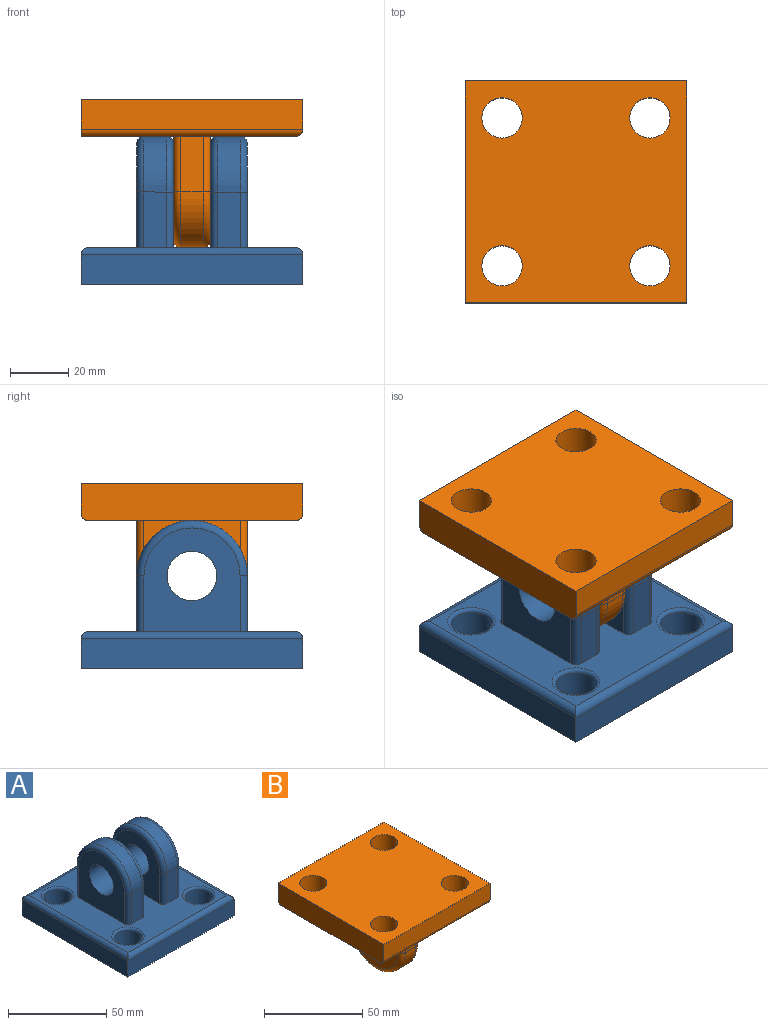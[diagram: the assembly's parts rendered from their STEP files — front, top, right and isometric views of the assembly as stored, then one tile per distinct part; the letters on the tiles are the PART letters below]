
ASSEMBLY  parts=2 mates=1
PART A: 42 faces, bbox 76.2x76.2x52.4 mm
  f0: plane 19.05x7.62mm, normal (0,-1,0), area 145.2mm2, adj f3,f5,f27,f28
  f1: plane 19.05x7.62mm, normal (0,1,0), area 145.2mm2, adj f3,f5,f25,f30
  f2: cylinder r=19.05mm len=38.1mm, axis (1,0,0), area 456mm2, adj f16,f18,f23,f32
  f3: cylinder r=19.05mm len=38.1mm, axis (1,0,0), area 456mm2, adj f0,f1,f26,f29
  f4: cylinder r=8.54mm len=17.08mm, axis (1,0,0), area 681.5mm2, adj f15,f20
  f5: plane 71.12x71.12mm, normal (0,0,1), area 3258.5mm2, adj f0,f1,f15,f16,f17,f18,f20,f21
  f6: plane 76.2x10.16mm, normal (0,-1,0), area 774.2mm2, adj f7,f13,f14,f34
  f7: plane 76.2x10.16mm, normal (1,0,0), area 774.2mm2, adj f6,f8,f14,f35
  f8: plane 76.2x10.16mm, normal (0,1,0), area 774.2mm2, adj f7,f13,f14,f37
  f9: cylinder r=6.92mm len=13.84mm, axis (0,0,-1), area 497mm2, adj f14,f41
  f10: cylinder r=6.92mm len=13.84mm, axis (0,0,-1), area 497mm2, adj f14,f40
  f11: cylinder r=6.92mm len=13.84mm, axis (0,0,-1), area 497mm2, adj f14,f39
  f12: cylinder r=6.92mm len=13.84mm, axis (0,0,-1), area 497mm2, adj f14,f38
  f13: plane 76.2x10.16mm, normal (-1,0,0), area 774.2mm2, adj f6,f8,f14,f36
  f14: plane 76.2x76.2mm, normal (0,0,-1), area 5204.7mm2, adj f6,f7,f8,f9,f10,f11,f12,f13
  f15: plane 35.56x33.02mm, normal (-1,0,0), area 828.1mm2, adj f4,f5,f31,f32,f33
  f16: plane 19.05x7.62mm, normal (0,-1,0), area 145.2mm2, adj f2,f5,f24,f31
  f17: plane 35.56x33.02mm, normal (1,0,0), area 828.1mm2, adj f5,f19,f28,f29,f30
  f18: plane 19.05x7.62mm, normal (0,1,0), area 145.2mm2, adj f2,f5,f22,f33
  f19: cylinder r=8.54mm len=17.08mm, axis (1,0,0), area 681.5mm2, adj f17,f21
  f20: plane 35.56x33.02mm, normal (1,0,0), area 828.1mm2, adj f4,f5,f22,f23,f24
  f21: plane 35.56x33.02mm, normal (-1,0,0), area 828.1mm2, adj f5,f19,f25,f26,f27
  f22: cylinder r=2.54mm len=19.05mm, axis (0,0,1), area 76mm2, adj f5,f18,f20,f23
  f23: torus R=16.51mm, axis (1,0,0), area 227.2mm2, adj f2,f20,f22,f24
  f24: cylinder r=2.54mm len=19.05mm, axis (0,0,-1), area 76mm2, adj f5,f16,f20,f23
  f25: cylinder r=2.54mm len=19.05mm, axis (0,0,-1), area 76mm2, adj f1,f5,f21,f26
  f26: torus R=16.51mm, axis (1,0,0), area 227.2mm2, adj f3,f21,f25,f27
  f27: cylinder r=2.54mm len=19.05mm, axis (0,0,1), area 76mm2, adj f0,f5,f21,f26
  f28: cylinder r=2.54mm len=19.05mm, axis (0,0,-1), area 76mm2, adj f0,f5,f17,f29
  f29: torus R=16.51mm, axis (-1,0,0), area 227.2mm2, adj f3,f17,f28,f30
  f30: cylinder r=2.54mm len=19.05mm, axis (0,0,1), area 76mm2, adj f1,f5,f17,f29
  f31: cylinder r=2.54mm len=19.05mm, axis (0,0,1), area 76mm2, adj f5,f15,f16,f32
  f32: torus R=16.51mm, axis (-1,0,0), area 227.2mm2, adj f2,f15,f31,f33
  f33: cylinder r=2.54mm len=19.05mm, axis (0,0,-1), area 76mm2, adj f5,f15,f18,f32
  f34: cylinder r=2.54mm len=76.2mm, axis (-1,0,0), area 296.7mm2, adj f5,f6,f35,f36
  f35: cylinder r=2.54mm len=76.2mm, axis (0,-1,0), area 296.7mm2, adj f5,f7,f34,f37
  f36: cylinder r=2.54mm len=76.2mm, axis (0,1,0), area 296.7mm2, adj f5,f13,f34,f37
  f37: cylinder r=2.54mm len=76.2mm, axis (1,0,0), area 296.7mm2, adj f5,f8,f35,f36
  f38: torus R=8.19mm, axis (0,0,1), area 92.5mm2, adj f5,f12
  f39: torus R=8.19mm, axis (0,0,1), area 92.5mm2, adj f5,f11
  f40: torus R=8.19mm, axis (0,0,1), area 92.5mm2, adj f5,f10
  f41: torus R=8.19mm, axis (0,0,1), area 92.5mm2, adj f5,f9
PART B: 29 faces, bbox 76.2x76.2x52.4 mm
  f0: plane 76.2x10.16mm, normal (0,-1,0), area 774.2mm2, adj f1,f7,f9,f26
  f1: plane 76.2x10.16mm, normal (1,0,0), area 774.2mm2, adj f0,f2,f9,f27
  f2: plane 76.2x10.16mm, normal (0,1,0), area 774.2mm2, adj f1,f7,f9,f28
  f3: cylinder r=6.92mm len=13.84mm, axis (0,0,1), area 441.7mm2, adj f9,f25
  f4: cylinder r=6.92mm len=13.84mm, axis (0,0,1), area 441.7mm2, adj f9,f24
  f5: cylinder r=6.92mm len=13.84mm, axis (0,0,1), area 441.7mm2, adj f9,f23
  f6: cylinder r=6.92mm len=13.84mm, axis (0,0,1), area 441.7mm2, adj f9,f22
  f7: plane 76.2x12.7mm, normal (-1,0,0), area 965mm2, adj f0,f2,f8,f9,f26,f28
  f8: plane 73.66x71.12mm, normal (0,0,-1), area 3635.8mm2, adj f7,f10,f11,f12,f13,f16,f18,f19
  f9: plane 76.2x76.2mm, normal (0,0,1), area 5204.7mm2, adj f0,f1,f2,f3,f4,f5,f6,f7
  f10: plane 35.56x33.02mm, normal (-1,0,0), area 828.1mm2, adj f8,f15,f19,f20,f21
  f11: plane 19.05x7.62mm, normal (0,1,0), area 145.2mm2, adj f8,f14,f16,f19
  f12: plane 35.56x33.02mm, normal (1,0,0), area 828.1mm2, adj f8,f15,f16,f17,f18
  f13: plane 19.05x7.62mm, normal (0,-1,0), area 145.2mm2, adj f8,f14,f18,f21
  f14: cylinder r=19.05mm len=38.1mm, axis (1,0,0), area 456mm2, adj f11,f13,f17,f20
  f15: cylinder r=8.54mm len=17.08mm, axis (1,0,0), area 681.5mm2, adj f10,f12
  f16: cylinder r=2.54mm len=19.05mm, axis (0,0,1), area 76mm2, adj f8,f11,f12,f17
  f17: torus R=16.51mm, axis (-1,0,0), area 227.2mm2, adj f12,f14,f16,f18
  f18: cylinder r=2.54mm len=19.05mm, axis (0,0,-1), area 76mm2, adj f8,f12,f13,f17
  f19: cylinder r=2.54mm len=19.05mm, axis (0,0,-1), area 76mm2, adj f8,f10,f11,f20
  f20: torus R=16.51mm, axis (-1,0,0), area 227.2mm2, adj f10,f14,f19,f21
  f21: cylinder r=2.54mm len=19.05mm, axis (0,0,1), area 76mm2, adj f8,f10,f13,f20
  f22: torus R=9.46mm, axis (0,0,1), area 196.6mm2, adj f6,f8
  f23: torus R=9.46mm, axis (0,0,1), area 196.6mm2, adj f5,f8
  f24: torus R=9.46mm, axis (0,0,1), area 196.6mm2, adj f4,f8
  f25: torus R=9.46mm, axis (0,0,1), area 196.6mm2, adj f3,f8
  f26: cylinder r=2.54mm len=76.2mm, axis (-1,0,0), area 300.3mm2, adj f0,f7,f8,f27
  f27: cylinder r=2.54mm len=76.2mm, axis (0,-1,0), area 296.7mm2, adj f1,f8,f26,f28
  f28: cylinder r=2.54mm len=76.2mm, axis (1,0,0), area 300.3mm2, adj f2,f7,f8,f27
PLACE A t=(23.89,-22.48,-3.55)mm
PLACE B t=(23.89,-22.48,59.95)mm
MATE pin_slot A.f29 <-> B.f20  axis (-1,0,0) through (30.24,-22.48,28.2)mm
